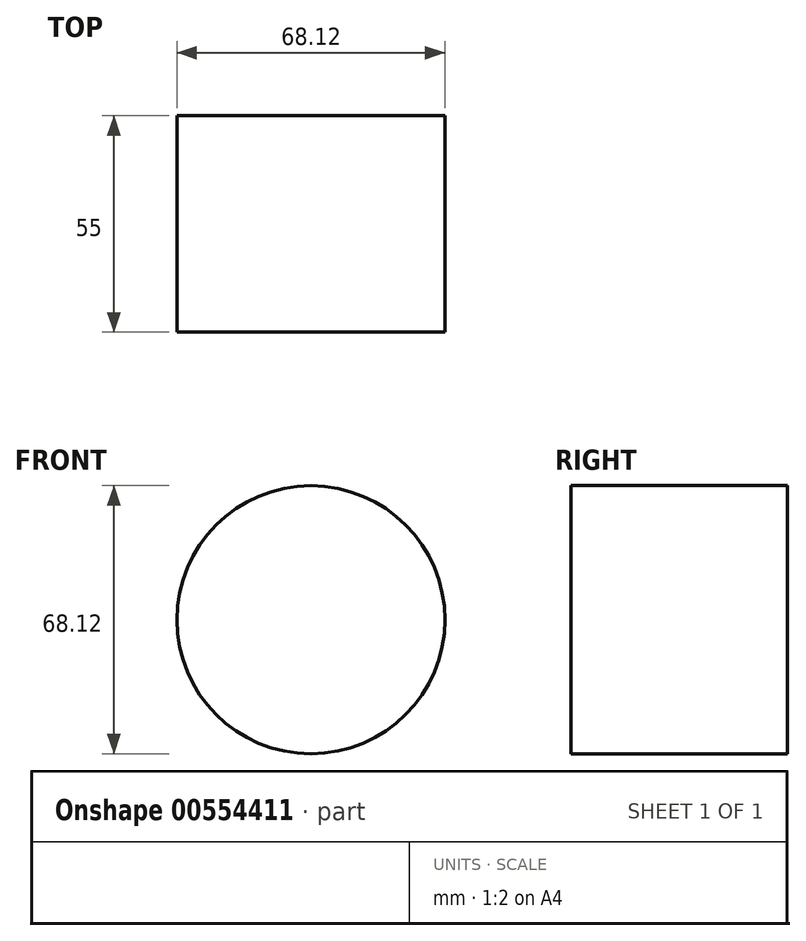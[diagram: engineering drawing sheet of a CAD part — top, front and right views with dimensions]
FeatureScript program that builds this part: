
annotation { "Feature Type Name" : "Feature", "Feature Type Description" : "" }
export const myFeature = defineFeature(function(context is Context, id is Id, definition is map)
    precondition{}
    {
        {
            var Q0;
            Q0=qCreatedBy(makeId("Front.planeOp"),FACE);
            var sketch = newSketch(context, id + "F0", { "sketchPlane" : qUnion([Q0])});
            skCircle(sketch, "E0", {"center": v(-9.3, 8.1) * mm, "radius": 34.06 * mm});
            skSolve(sketch);
        }
        {
            var Q0;
            Q0=sQuery(id+"F0.wireOp",EDGE,"E0");
            extrude(context, id + "F1", {"bodyType" : ToolBodyType.SURFACE, "surfaceEntities" : qUnion([Q0]), "depth" : 55 * mm, "offsetDistance" : 25 * mm});
        }
    });
